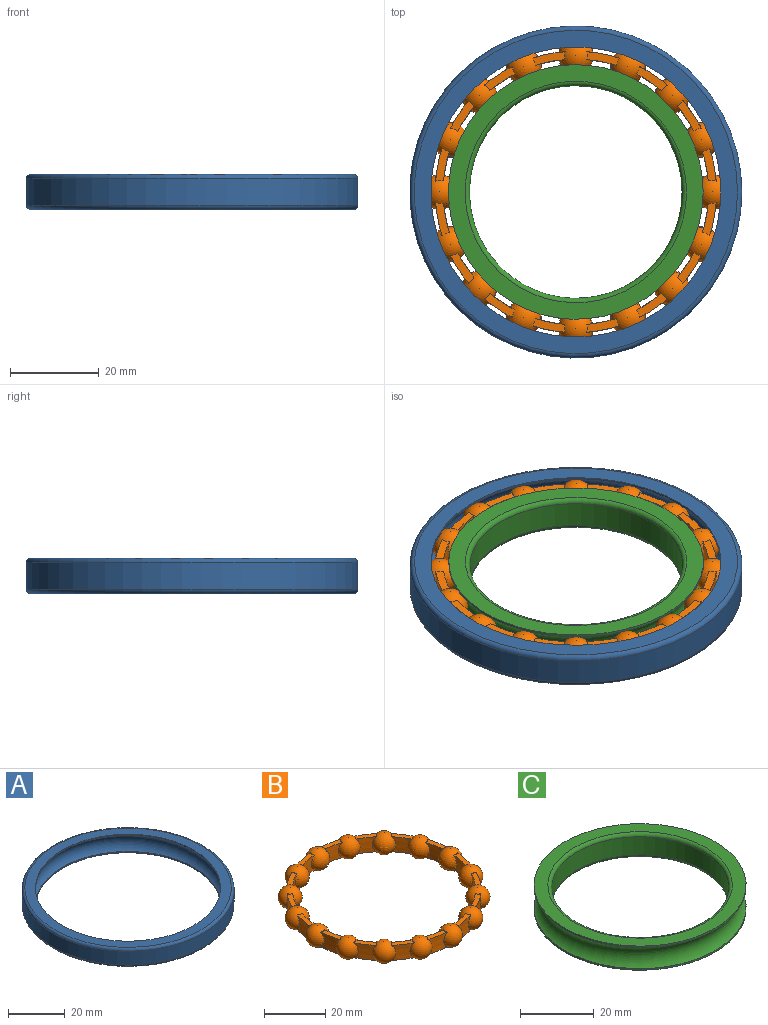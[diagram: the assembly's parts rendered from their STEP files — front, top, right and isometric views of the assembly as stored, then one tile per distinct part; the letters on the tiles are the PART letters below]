
ASSEMBLY  parts=3 mates=1
PART A: 8 faces, bbox 81.2x81.2x8 mm
  f0: torus R=30.75mm, axis (0,0,1), area 1792.7mm2, adj f1,f7
  f1: cylinder r=32.75mm len=65.5mm, axis (0,0,1), area 110.3mm2, adj f0,f2
  f2: plane 73x73mm, normal (0,0,-1), area 815.8mm2, adj f1,f3
  f3: torus R=36.5mm, axis (0,0,1), area 366.5mm2, adj f2,f4
  f4: cylinder r=37.5mm len=75mm, axis (0,0,1), area 1413.7mm2, adj f3,f5
  f5: torus R=36.5mm, axis (0,0,1), area 366.5mm2, adj f4,f6
  f6: plane 73x73mm, normal (0,0,1), area 815.8mm2, adj f5,f7
  f7: cylinder r=32.75mm len=65.5mm, axis (0,0,1), area 110.3mm2, adj f0,f6
PART B: 80 faces, bbox 69.4x69.4x7.9 mm
  f0: cylinder r=30mm len=6.78mm, axis (0,0,-1), area 29.8mm2, adj f4,f5,f64,f79
  f1: cylinder r=30mm len=6.78mm, axis (0,0,-1), area 29.8mm2, adj f8,f9,f78,f79
  f2: cylinder r=31.77mm len=7.52mm, axis (0,0,-1), area 33.7mm2, adj f4,f5,f64,f79
  f3: cylinder r=31.77mm len=7.52mm, axis (0,0,-1), area 33.7mm2, adj f8,f9,f78,f79
  f4: plane 7.52x3.13mm, normal (0,0,1), area 12.6mm2, adj f0,f2,f64,f79
  f5: plane 7.52x3.13mm, normal (0,0,-1), area 12.6mm2, adj f0,f2,f64,f79
  f6: cylinder r=30mm len=6mm, axis (0,0,-1), area 29.8mm2, adj f12,f13,f77,f78
  f7: cylinder r=31.77mm len=6.37mm, axis (0,0,-1), area 33.7mm2, adj f12,f13,f77,f78
  f8: plane 7.52x3.13mm, normal (0,0,1), area 12.6mm2, adj f1,f3,f78,f79
  f9: plane 7.52x3.13mm, normal (0,0,-1), area 12.6mm2, adj f1,f3,f78,f79
  f10: cylinder r=30mm len=6mm, axis (0,0,-1), area 29.8mm2, adj f16,f17,f76,f77
  f11: cylinder r=31.77mm len=6.37mm, axis (0,0,-1), area 33.7mm2, adj f16,f17,f76,f77
  f12: plane 7.03x5.5mm, normal (0,0,1), area 12.6mm2, adj f6,f7,f77,f78
  f13: plane 7.03x5.5mm, normal (0,0,-1), area 12.6mm2, adj f6,f7,f77,f78
  f14: cylinder r=30mm len=6.78mm, axis (0,0,-1), area 29.8mm2, adj f52,f53,f75,f76
  f15: cylinder r=31.77mm len=7.52mm, axis (0,0,-1), area 33.7mm2, adj f52,f53,f75,f76
  f16: plane 7.03x5.5mm, normal (0,0,1), area 12.6mm2, adj f10,f11,f76,f77
  f17: plane 7.03x5.5mm, normal (0,0,-1), area 12.6mm2, adj f10,f11,f76,f77
  f18: cylinder r=30mm len=6.78mm, axis (0,0,-1), area 29.8mm2, adj f20,f21,f74,f75
  f19: cylinder r=31.77mm len=7.52mm, axis (0,0,-1), area 33.7mm2, adj f20,f21,f74,f75
  f20: plane 7.52x3.13mm, normal (0,0,1), area 12.6mm2, adj f18,f19,f74,f75
  f21: plane 7.52x3.13mm, normal (0,0,-1), area 12.6mm2, adj f18,f19,f74,f75
  f22: cylinder r=30mm len=6mm, axis (0,0,-1), area 29.8mm2, adj f24,f25,f73,f74
  f23: cylinder r=31.77mm len=6.37mm, axis (0,0,-1), area 33.7mm2, adj f24,f25,f73,f74
  f24: plane 7.03x5.5mm, normal (0,0,1), area 12.6mm2, adj f22,f23,f73,f74
  f25: plane 7.03x5.5mm, normal (0,0,-1), area 12.6mm2, adj f22,f23,f73,f74
  f26: cylinder r=30mm len=6mm, axis (0,0,-1), area 29.8mm2, adj f28,f29,f72,f73
  f27: cylinder r=31.77mm len=6.37mm, axis (0,0,-1), area 33.7mm2, adj f28,f29,f72,f73
  f28: plane 7.03x5.5mm, normal (0,0,1), area 12.6mm2, adj f26,f27,f72,f73
  f29: plane 7.03x5.5mm, normal (0,0,-1), area 12.6mm2, adj f26,f27,f72,f73
  f30: cylinder r=30mm len=6.78mm, axis (0,0,-1), area 29.8mm2, adj f32,f33,f71,f72
  f31: cylinder r=31.77mm len=7.52mm, axis (0,0,-1), area 33.7mm2, adj f32,f33,f71,f72
  f32: plane 7.52x3.13mm, normal (0,0,1), area 12.6mm2, adj f30,f31,f71,f72
  f33: plane 7.52x3.13mm, normal (0,0,-1), area 12.6mm2, adj f30,f31,f71,f72
  f34: cylinder r=30mm len=6.78mm, axis (0,0,-1), area 29.8mm2, adj f36,f37,f70,f71
  f35: cylinder r=31.77mm len=7.52mm, axis (0,0,-1), area 33.7mm2, adj f36,f37,f70,f71
  f36: plane 7.52x3.13mm, normal (0,0,1), area 12.6mm2, adj f34,f35,f70,f71
  f37: plane 7.52x3.13mm, normal (0,0,-1), area 12.6mm2, adj f34,f35,f70,f71
  f38: cylinder r=30mm len=6mm, axis (0,0,-1), area 29.8mm2, adj f40,f41,f69,f70
  f39: cylinder r=31.77mm len=6.37mm, axis (0,0,-1), area 33.7mm2, adj f40,f41,f69,f70
  f40: plane 7.03x5.5mm, normal (0,0,1), area 12.6mm2, adj f38,f39,f69,f70
  f41: plane 7.03x5.5mm, normal (0,0,-1), area 12.6mm2, adj f38,f39,f69,f70
  f42: cylinder r=30mm len=6mm, axis (0,0,-1), area 29.8mm2, adj f44,f45,f68,f69
  f43: cylinder r=31.77mm len=6.37mm, axis (0,0,-1), area 33.7mm2, adj f44,f45,f68,f69
  f44: plane 7.03x5.5mm, normal (0,0,1), area 12.6mm2, adj f42,f43,f68,f69
  f45: plane 7.03x5.5mm, normal (0,0,-1), area 12.6mm2, adj f42,f43,f68,f69
  f46: cylinder r=30mm len=6.78mm, axis (0,0,-1), area 29.8mm2, adj f48,f49,f67,f68
  f47: cylinder r=31.77mm len=7.52mm, axis (0,0,-1), area 33.7mm2, adj f48,f49,f67,f68
  f48: plane 7.52x3.13mm, normal (0,0,1), area 12.6mm2, adj f46,f47,f67,f68
  f49: plane 7.52x3.13mm, normal (0,0,-1), area 12.6mm2, adj f46,f47,f67,f68
  f50: cylinder r=30mm len=6.78mm, axis (0,0,-1), area 29.8mm2, adj f56,f57,f66,f67
  f51: cylinder r=31.77mm len=7.52mm, axis (0,0,-1), area 33.7mm2, adj f56,f57,f66,f67
  f52: plane 7.52x3.13mm, normal (0,0,1), area 12.6mm2, adj f14,f15,f75,f76
  f53: plane 7.52x3.13mm, normal (0,0,-1), area 12.6mm2, adj f14,f15,f75,f76
  f54: cylinder r=30mm len=6mm, axis (0,0,-1), area 29.8mm2, adj f60,f61,f65,f66
  f55: cylinder r=31.77mm len=6.37mm, axis (0,0,-1), area 33.7mm2, adj f60,f61,f65,f66
  f56: plane 7.52x3.13mm, normal (0,0,1), area 12.6mm2, adj f50,f51,f66,f67
  f57: plane 7.52x3.13mm, normal (0,0,-1), area 12.6mm2, adj f50,f51,f66,f67
  f58: cylinder r=30mm len=6mm, axis (0,0,-1), area 29.8mm2, adj f62,f63,f64,f65
  f59: cylinder r=31.77mm len=6.37mm, axis (0,0,-1), area 33.7mm2, adj f62,f63,f64,f65
  f60: plane 7.03x5.5mm, normal (0,0,1), area 12.6mm2, adj f54,f55,f65,f66
  f61: plane 7.03x5.5mm, normal (0,0,-1), area 12.6mm2, adj f54,f55,f65,f66
  f62: plane 7.03x5.5mm, normal (0,0,1), area 12.6mm2, adj f58,f59,f64,f65
  f63: plane 7.03x5.5mm, normal (0,0,-1), area 12.6mm2, adj f58,f59,f64,f65
  f64: sphere r=3.95mm, area 171.5mm2, adj f0,f2,f4,f5,f58,f59,f62,f63
  f65: sphere r=3.95mm, area 171.5mm2, adj f54,f55,f58,f59,f60,f61,f62,f63
  f66: sphere r=3.95mm, area 171.5mm2, adj f50,f51,f54,f55,f56,f57,f60,f61
  f67: sphere r=3.95mm, area 171.5mm2, adj f46,f47,f48,f49,f50,f51,f56,f57
  f68: sphere r=3.95mm, area 171.5mm2, adj f42,f43,f44,f45,f46,f47,f48,f49
  f69: sphere r=3.95mm, area 171.5mm2, adj f38,f39,f40,f41,f42,f43,f44,f45
  f70: sphere r=3.95mm, area 171.5mm2, adj f34,f35,f36,f37,f38,f39,f40,f41
  f71: sphere r=3.95mm, area 171.5mm2, adj f30,f31,f32,f33,f34,f35,f36,f37
  f72: sphere r=3.95mm, area 171.5mm2, adj f26,f27,f28,f29,f30,f31,f32,f33
  f73: sphere r=3.95mm, area 171.5mm2, adj f22,f23,f24,f25,f26,f27,f28,f29
  f74: sphere r=3.95mm, area 171.5mm2, adj f18,f19,f20,f21,f22,f23,f24,f25
  f75: sphere r=3.95mm, area 171.5mm2, adj f14,f15,f18,f19,f20,f21,f52,f53
  f76: sphere r=3.95mm, area 171.5mm2, adj f10,f11,f14,f15,f16,f17,f52,f53
  f77: sphere r=3.95mm, area 171.5mm2, adj f6,f7,f10,f11,f12,f13,f16,f17
  f78: sphere r=3.95mm, area 171.5mm2, adj f1,f3,f6,f7,f8,f9,f12,f13
  f79: sphere r=3.95mm, area 171.5mm2, adj f0,f1,f2,f3,f4,f5,f8,f9
PART C: 8 faces, bbox 66.6x66.6x8 mm
  f0: plane 57.5x57.5mm, normal (0,0,1), area 633.2mm2, adj f1,f7
  f1: torus R=25mm, axis (0,0,1), area 240.5mm2, adj f0,f2
  f2: cylinder r=24mm len=48mm, axis (0,0,1), area 904.8mm2, adj f1,f3
  f3: torus R=25mm, axis (0,0,1), area 240.5mm2, adj f2,f4
  f4: plane 57.5x57.5mm, normal (0,0,-1), area 633.2mm2, adj f3,f5
  f5: cylinder r=28.75mm len=57.5mm, axis (0,0,1), area 96.8mm2, adj f4,f6
  f6: torus R=30.75mm, axis (0,0,1), area 1444.5mm2, adj f5,f7
  f7: cylinder r=28.75mm len=57.5mm, axis (0,0,1), area 96.8mm2, adj f0,f6
PLACE A t=(1.14,0.41,-0.37)mm
PLACE B t=(1.14,0.41,-0.37)mm
PLACE C rot(axis=(1,0,0),180deg) t=(1.14,0.41,-0.37)mm
MATE revolute C.f1 <-> A.f0  axis (0,0,-1) through (1.14,0.41,-0.37)mm
